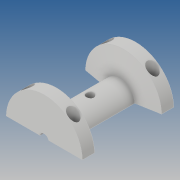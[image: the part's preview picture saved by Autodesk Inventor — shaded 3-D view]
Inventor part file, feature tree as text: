
AUTODESK INVENTOR PART (.ipt)
format: ipt  version: 2019 (Build 230136000, 136)  size: 176,128 bytes
history: native  units: mm
features: projected_geometry x5, sketch x4, other x2, extrude x2, hole x1
ambient origin geometry x8: Origin, YZ Plane, XZ Plane, XY Plane, X Axis, Y Axis, Z Axis, Center Point
bodies: Solide1 (feature_tree)
feature tree (14):
  other  "Révolution1"
  extrude  "Extrusion1"  Depth=5.75mm
  extrude  "Extrusion2"  Depth=50.0mm
  other  "Plan de construction2"
  hole  "Perçage2"  [1 undecoded]
  sketch  "Esquisse1"
  sketch  "Esquisse2"
  sketch  "Esquisse3"
  projected_geometry  "Boucle projetée1"
  projected_geometry  "Boucle projetée2"
  projected_geometry  "Boucle projetée3"
  sketch  "Esquisse6"
  projected_geometry  "Boucle projetée6"
  projected_geometry  "Boucle projetée7"
note: 1 required parameter value undecoded (feature->parameter linkage not recoverable at this tier; creation-order binding heuristic only, values carry confidence <= 0.55)
